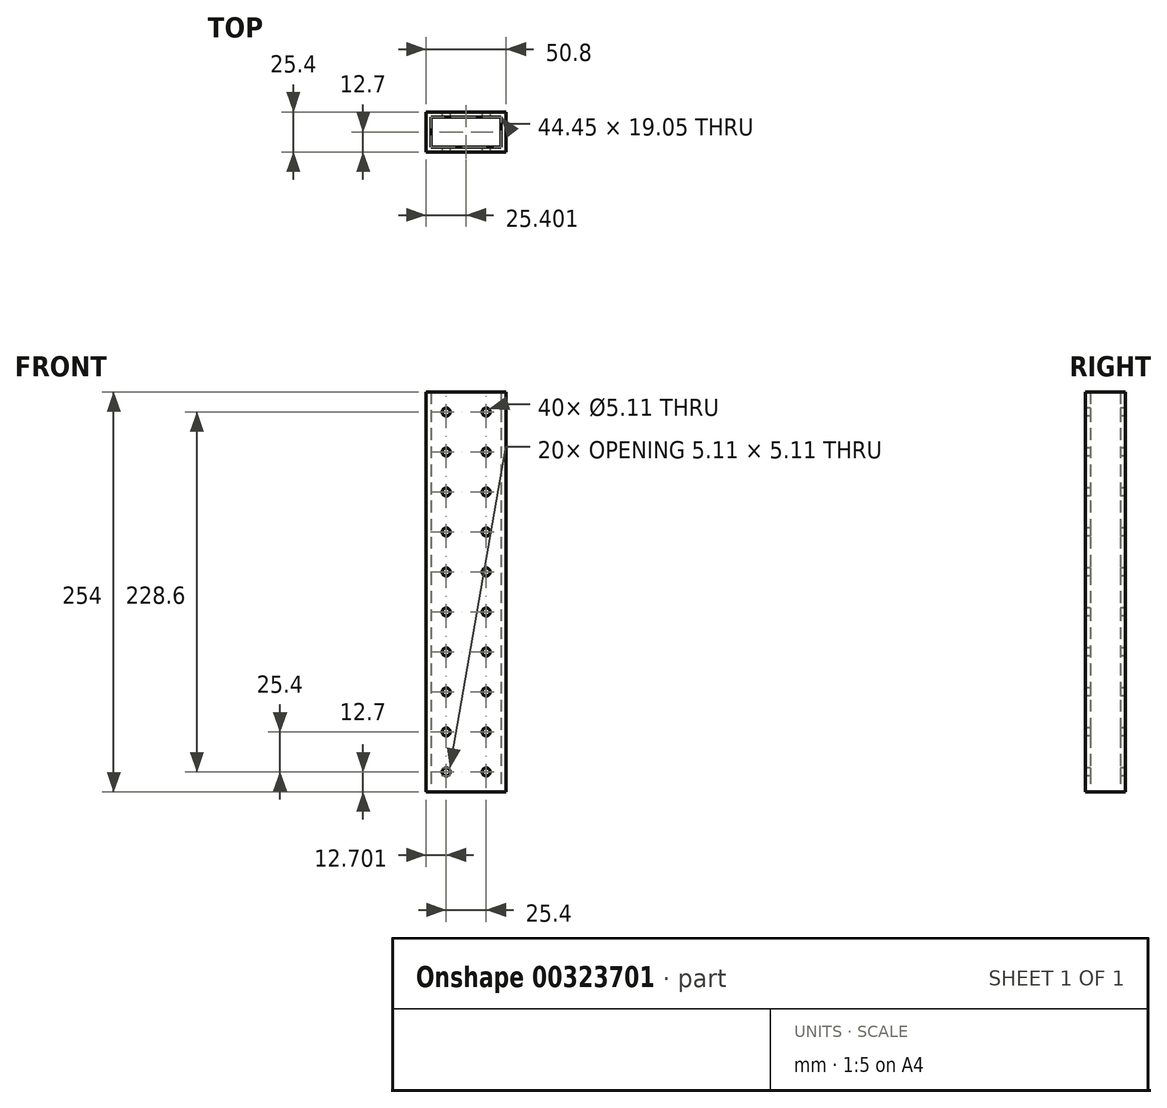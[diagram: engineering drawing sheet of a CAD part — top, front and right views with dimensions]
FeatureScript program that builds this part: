
annotation { "Feature Type Name" : "Feature", "Feature Type Description" : "" }
export const myFeature = defineFeature(function(context is Context, id is Id, definition is map)
    precondition{}
    {
        {
            var Q0;
            Q0=qCreatedBy(makeId("Top.planeOp"),FACE);
            var sketch = newSketch(context, id + "F0", { "sketchPlane" : qUnion([Q0])});
            skLineSegment(sketch, "E0.bottom", {"start": v(-28.89, 24.94) * mm, "end": v(21.91, 24.94) * mm});
            skLineSegment(sketch, "E0.top", {"start": v(-28.89, -0.46) * mm, "end": v(21.91, -0.46) * mm});
            skLineSegment(sketch, "E0.left", {"start": v(-28.89, 24.94) * mm, "end": v(-28.89, -0.46) * mm});
            skLineSegment(sketch, "E0.right", {"start": v(21.91, 24.94) * mm, "end": v(21.91, -0.46) * mm});
            skSolve(sketch);
        }
        {
            var Q0;
            Q0 = qSketchRegion(id + "F0", true);
            extrude(context, id + "F1", {"entities" : qUnion([Q0]), "depth" : 254 * mm});
        }
        {
            var Q0;
            Q0=makeQuery(id+"F1.opExtrude","SWEPT_FACE",FACE,{"disambiguationData":[OSD([sQuery(id+"F0.wireOp",EDGE,"E0.top")])]});
            var sketch = newSketch(context, id + "F2", { "sketchPlane" : qUnion([Q0])});
            skCircle(sketch, "E1", {"center": v(-16.19, 241.3) * mm, "radius": 2.55 * mm});
            skCircle(sketch, "E2.0.1.0", {"center": v(-16.19, 215.9) * mm, "radius": 2.55 * mm});
            skCircle(sketch, "E2.0.2.0", {"center": v(-16.19, 190.5) * mm, "radius": 2.55 * mm});
            skCircle(sketch, "E2.0.3.0", {"center": v(-16.19, 165.1) * mm, "radius": 2.55 * mm});
            skCircle(sketch, "E2.0.4.0", {"center": v(-16.19, 139.7) * mm, "radius": 2.55 * mm});
            skCircle(sketch, "E2.0.5.0", {"center": v(-16.19, 114.3) * mm, "radius": 2.55 * mm});
            skCircle(sketch, "E2.0.6.0", {"center": v(-16.19, 88.9) * mm, "radius": 2.55 * mm});
            skCircle(sketch, "E2.0.7.0", {"center": v(-16.19, 63.5) * mm, "radius": 2.55 * mm});
            skCircle(sketch, "E2.0.8.0", {"center": v(-16.19, 38.1) * mm, "radius": 2.55 * mm});
            skCircle(sketch, "E2.0.9.0", {"center": v(-16.19, 12.7) * mm, "radius": 2.55 * mm});
            skCircle(sketch, "E2.1.0.0", {"center": v(9.21, 241.3) * mm, "radius": 2.55 * mm});
            skCircle(sketch, "E2.1.1.0", {"center": v(9.21, 215.9) * mm, "radius": 2.55 * mm});
            skCircle(sketch, "E2.1.2.0", {"center": v(9.21, 190.5) * mm, "radius": 2.55 * mm});
            skCircle(sketch, "E2.1.3.0", {"center": v(9.21, 165.1) * mm, "radius": 2.55 * mm});
            skCircle(sketch, "E2.1.4.0", {"center": v(9.21, 139.7) * mm, "radius": 2.55 * mm});
            skCircle(sketch, "E2.1.5.0", {"center": v(9.21, 114.3) * mm, "radius": 2.55 * mm});
            skCircle(sketch, "E2.1.6.0", {"center": v(9.21, 88.9) * mm, "radius": 2.55 * mm});
            skCircle(sketch, "E2.1.7.0", {"center": v(9.21, 63.5) * mm, "radius": 2.55 * mm});
            skCircle(sketch, "E2.1.8.0", {"center": v(9.21, 38.1) * mm, "radius": 2.55 * mm});
            skCircle(sketch, "E2.1.9.0", {"center": v(9.21, 12.7) * mm, "radius": 2.55 * mm});
            skLineSegment(sketch, "E2.direction1", {"start": v(-16.19, 241.3) * mm, "end": v(9.21, 241.3) * mm, "construction": true});
            skLineSegment(sketch, "E2.direction2", {"start": v(-16.19, 241.3) * mm, "end": v(-16.19, 215.9) * mm, "construction": true});
            skSolve(sketch);
        }
        {
            var Q0;
            Q0 = qSketchRegion(id + "F2", true);
            extrude(context, id + "F3", {"entities" : qUnion([Q0]), "operationType" : NewBodyOperationType.REMOVE, "oppositeDirection" : true, "depth" : 25.4 * mm});
        }
        {
            var Q0;
            Q0=makeQuery(id+"F1.opExtrude","CAP_FACE",FACE,{"disambiguationData":[OSD([sQuery(id+"F0.wireOp",EDGE,"E0.bottom"),sQuery(id+"F0.wireOp",EDGE,"E0.top"),sQuery(id+"F0.wireOp",EDGE,"E0.left"),sQuery(id+"F0.wireOp",EDGE,"E0.right")])],"isStart":true});
            var sketch = newSketch(context, id + "F4", { "sketchPlane" : qUnion([Q0])});
            skLineSegment(sketch, "E3.bottom", {"start": v(-25.71, -2.71) * mm, "end": v(18.74, -2.71) * mm});
            skLineSegment(sketch, "E3.top", {"start": v(-25.71, -21.76) * mm, "end": v(18.74, -21.76) * mm});
            skLineSegment(sketch, "E3.left", {"start": v(-25.71, -2.71) * mm, "end": v(-25.71, -21.76) * mm});
            skLineSegment(sketch, "E3.right", {"start": v(18.74, -2.71) * mm, "end": v(18.74, -21.76) * mm});
            skSolve(sketch);
        }
        {
            var Q0;
            Q0 = qSketchRegion(id + "F4", true);
            extrude(context, id + "F5", {"entities" : qUnion([Q0]), "operationType" : NewBodyOperationType.REMOVE, "oppositeDirection" : true, "depth" : 254 * mm});
        }
    });
